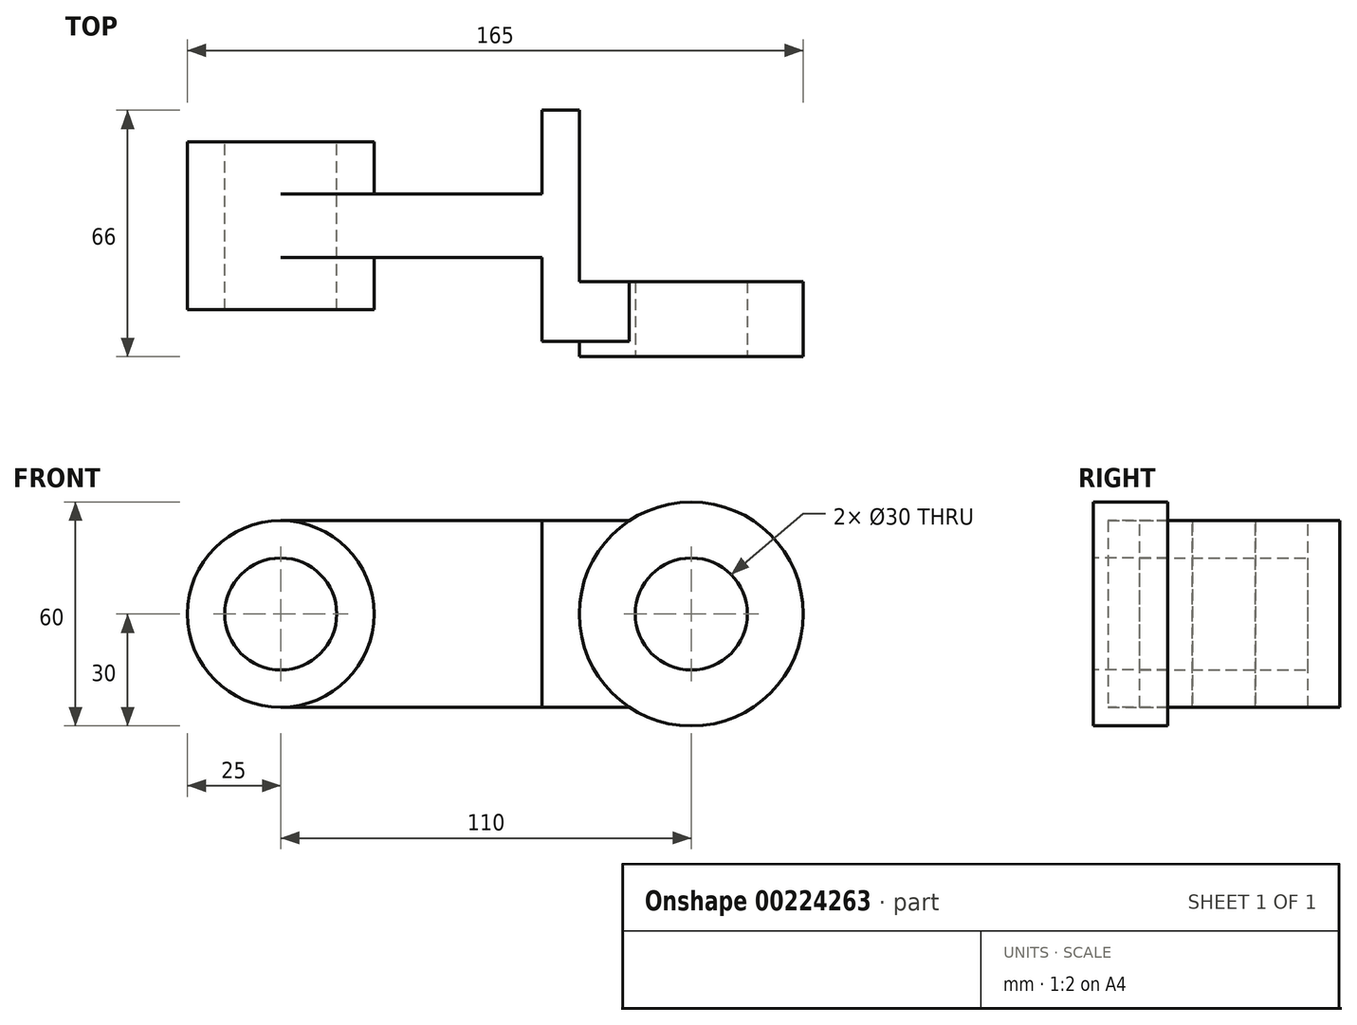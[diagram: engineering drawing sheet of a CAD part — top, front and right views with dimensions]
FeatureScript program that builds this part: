
annotation { "Feature Type Name" : "Feature", "Feature Type Description" : "" }
export const myFeature = defineFeature(function(context is Context, id is Id, definition is map)
    precondition{}
    {
        {
            var Q0;
            Q0=qCreatedBy(makeId("Front.planeOp"),FACE);
            var sketch = newSketch(context, id + "F0", { "sketchPlane" : qUnion([Q0])});
            skCircle(sketch, "E0", {"center": v(0, 0) * mm, "radius": 25 * mm});
            skCircle(sketch, "E1", {"center": v(0, 0) * mm, "radius": 15 * mm});
            skLineSegment(sketch, "E2", {"start": v(0, 25) * mm, "end": v(70, 25) * mm});
            skLineSegment(sketch, "E3", {"start": v(70, 25) * mm, "end": v(70, -25) * mm});
            skLineSegment(sketch, "E4", {"start": v(70, -25) * mm, "end": v(0, -25) * mm});
            skSolve(sketch);
        }
        {
            var Q0;
            Q0=makeQuery(id+"F0.imprint","IMPRINT",FACE,{"disambiguationData":[TD([[makeQuery(id+"F0.imprint","IMPRINT",EDGE,{"derivedFrom":sQuery(id+"F0.wireOp",EDGE,"E1")}),-1.0]])]});
            extrude(context, id + "F1", {"entities" : qUnion([Q0]), "endBound" : BoundingType.SYMMETRIC, "depth" : 45 * mm});
        }
        {
            var Q0;
            {var subQ0=sQuery(id+"F0.wireOp",EDGE,"E2");Q0=makeQuery(id+"F0.imprint","IMPRINT",FACE,{"disambiguationData":[TD([[makeQuery(id+"F0.imprint","IMPRINT",EDGE,{"derivedFrom":subQ0}),-1.0]])]});}
            extrude(context, id + "F2", {"entities" : qUnion([Q0]), "operationType" : NewBodyOperationType.ADD, "endBound" : BoundingType.SYMMETRIC, "depth" : 17 * mm});
        }
        {
            var Q0;
            Q0=qCreatedBy(makeId("Front.planeOp"),FACE);
            var sketch = newSketch(context, id + "F3", { "sketchPlane" : qUnion([Q0])});
            skLineSegment(sketch, "E5", {"start": v(70, 25) * mm, "end": v(80, 25) * mm});
            skLineSegment(sketch, "E6", {"start": v(80, 25) * mm, "end": v(80, -25) * mm});
            skLineSegment(sketch, "E7", {"start": v(80, -25) * mm, "end": v(70, -25) * mm});
            skSolve(sketch);
        }
        {
            var Q0;
            Q0=qCreatedBy(makeId("Front.planeOp"),FACE);
            var sketch = newSketch(context, id + "F4", { "sketchPlane" : qUnion([Q0])});
            skPoint(sketch, "E8.0", {"position": v(75, 25) * mm});
            skLineSegment(sketch, "E9.0", {"start": v(70, 25) * mm, "end": v(80, 25) * mm});
            skLineSegment(sketch, "E10.0", {"start": v(80, 25) * mm, "end": v(80, -25) * mm});
            skLineSegment(sketch, "E11.0", {"start": v(80, -25) * mm, "end": v(70, -25) * mm});
            skSolve(sketch);
        }
        {
            var Q0;
            Q0=qCreatedBy(makeId("Front.planeOp"),FACE);
            var sketch = newSketch(context, id + "F5", { "sketchPlane" : qUnion([Q0])});
            skLineSegment(sketch, "E12.0", {"start": v(70, 25) * mm, "end": v(80, 25) * mm});
            skLineSegment(sketch, "E13.0", {"start": v(70, 25) * mm, "end": v(70, -25) * mm});
            skLineSegment(sketch, "E14.0", {"start": v(80, 25) * mm, "end": v(80, -25) * mm});
            skPoint(sketch, "E15.0", {"position": v(75, -25) * mm});
            skLineSegment(sketch, "E16.0", {"start": v(80, -25) * mm, "end": v(70, -25) * mm});
            skSolve(sketch);
        }
        {
            var Q0;
            Q0=makeQuery(id+"F5.imprint","IMPRINT",FACE,{"disambiguationData":[TD([[makeQuery(id+"F5.imprint","IMPRINT",EDGE,{"derivedFrom":sQuery(id+"F5.wireOp",EDGE,"E12.0")}),-1.0]])]});
            extrude(context, id + "F6", {"entities" : qUnion([Q0]), "operationType" : NewBodyOperationType.ADD, "endBound" : BoundingType.SYMMETRIC, "depth" : 62 * mm});
        }
        {
            var Q0;
            Q0=makeQuery(id+"F6.opExtrude","CAP_FACE",FACE,{"disambiguationData":[OSD([sQuery(id+"F5.wireOp",EDGE,"E12.0"),sQuery(id+"F5.wireOp",EDGE,"E13.0"),sQuery(id+"F5.wireOp",EDGE,"E14.0"),sQuery(id+"F5.wireOp",EDGE,"E16.0")])],"isStart":false});
            var sketch = newSketch(context, id + "F7", { "sketchPlane" : qUnion([Q0])});
            skSolve(sketch);
        }
        {
            var Q0;
            Q0=makeQuery(id+"F7.imprint","IMPRINT",FACE,{"disambiguationData":[TD([[makeQuery(id+"F7.imprint","IMPRINT",EDGE,{"derivedFrom":makeQuery(id+"F6.opExtrude","CAP_EDGE",EDGE,{"disambiguationData":[OSD([sQuery(id+"F5.wireOp",EDGE,"E12.0")])],"isStart":false})}),-1.0]])]});
            var sketch = newSketch(context, id + "F8", { "sketchPlane" : qUnion([Q0])});
            skLineSegment(sketch, "E17.0", {"start": v(70, 25) * mm, "end": v(80, 25) * mm});
            skLineSegment(sketch, "E18.0", {"start": v(70, 25) * mm, "end": v(70, -25) * mm});
            skLineSegment(sketch, "E19.0", {"start": v(80, 25) * mm, "end": v(80, -25) * mm});
            skPoint(sketch, "E20.0", {"position": v(75, -25) * mm});
            skLineSegment(sketch, "E21", {"start": v(80, 25) * mm, "end": v(93.42, 25) * mm});
            skLineSegment(sketch, "E22", {"start": v(80, -25) * mm, "end": v(93.42, -25) * mm});
            skCircle(sketch, "E23", {"center": v(110, 0) * mm, "radius": 30 * mm});
            skCircle(sketch, "E24", {"center": v(110, 0) * mm, "radius": 15 * mm});
            skSolve(sketch);
        }
        {
            var Q0;
            {var subQ0=sQuery(id+"F8.wireOp",EDGE,"E21");Q0=makeQuery(id+"F8.imprint","IMPRINT",FACE,{"disambiguationData":[TD([[makeQuery(id+"F8.imprint","IMPRINT",EDGE,{"derivedFrom":subQ0}),-1.0]])]});}
            var Q1;
            Q1=makeQuery(id+"F8.imprint","IMPRINT",FACE,{"disambiguationData":[TD([[makeQuery(id+"F8.imprint","IMPRINT",EDGE,{"derivedFrom":sQuery(id+"F8.wireOp",EDGE,"E24")}),-1.0]])]});
            var Q2;
            {var subQ0=sQuery(id+"F8.wireOp",EDGE,"E22");Q2=makeQuery(id+"F8.imprint","IMPRINT",FACE,{"disambiguationData":[TD([[makeQuery(id+"F8.imprint","IMPRINT",EDGE,{"derivedFrom":subQ0}),1.0]])]});}
            extrude(context, id + "F9", {"entities" : qUnion([Q0, Q1, Q2]), "operationType" : NewBodyOperationType.ADD, "oppositeDirection" : true, "depth" : 16 * mm});
        }
        {
            var Q0;
            Q0 = qSketchRegion(id + "F8", true);
            extrude(context, id + "F10", {"entities" : qUnion([Q0]), "operationType" : NewBodyOperationType.ADD, "oppositeDirection" : true, "depth" : 14 * mm});
        }
        {
            var Q0;
            Q0=makeQuery(id+"F8.imprint","IMPRINT",FACE,{"disambiguationData":[TD([[makeQuery(id+"F8.imprint","IMPRINT",EDGE,{"derivedFrom":sQuery(id+"F8.wireOp",EDGE,"E24")}),-1.0]])]});
            cPlane(context, id + "F11", {"entities" : qUnion([Q0]), "cplaneType" : CPlaneType.OFFSET, "offset" : 0 * mm, "width" : 150 * mm, "height" : 150 * mm});
        }
        {
            var Q0;
            Q0=makeQuery(id+"F8.imprint","IMPRINT",FACE,{"disambiguationData":[TD([[makeQuery(id+"F8.imprint","IMPRINT",EDGE,{"derivedFrom":sQuery(id+"F8.wireOp",EDGE,"E24")}),-1.0]])]});
            extrude(context, id + "F12", {"entities" : qUnion([Q0]), "operationType" : NewBodyOperationType.ADD, "depth" : 4 * mm});
        }
    });
